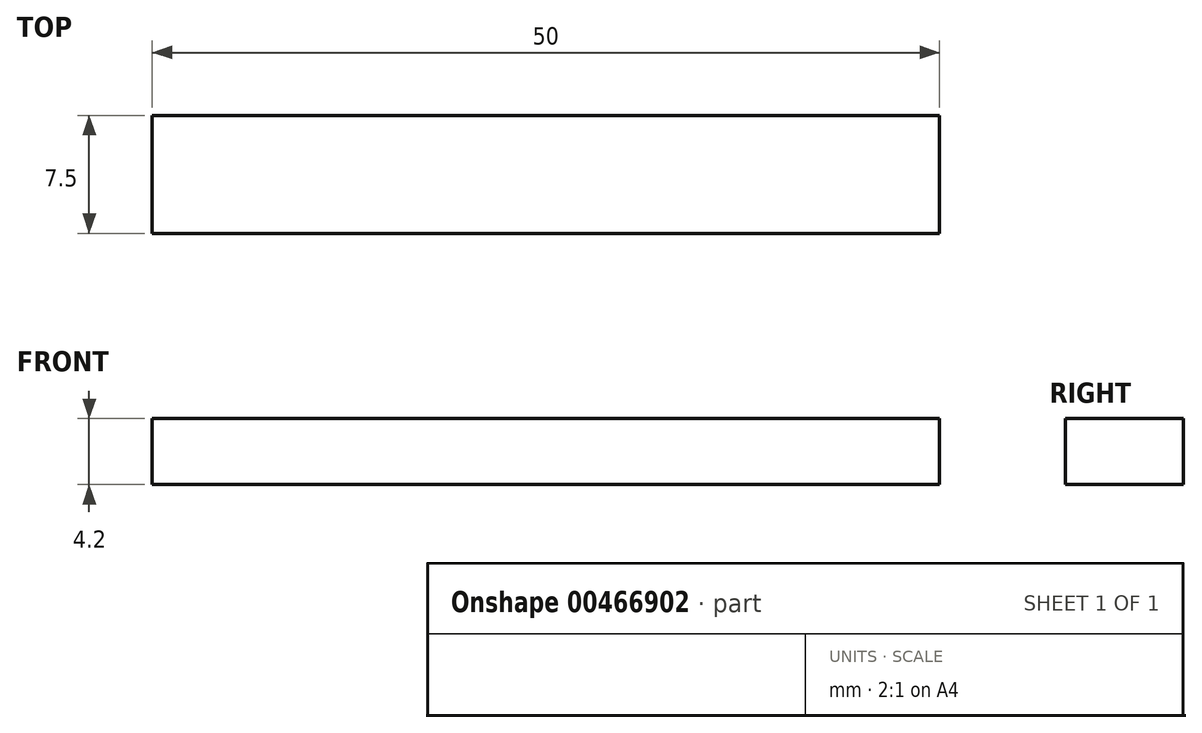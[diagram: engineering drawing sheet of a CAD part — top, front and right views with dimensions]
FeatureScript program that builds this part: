
annotation { "Feature Type Name" : "Feature", "Feature Type Description" : "" }
export const myFeature = defineFeature(function(context is Context, id is Id, definition is map)
    precondition{}
    {
        {
            var Q0;
            Q0=qCreatedBy(makeId("Top.planeOp"),FACE);
            var sketch = newSketch(context, id + "F0", { "sketchPlane" : qUnion([Q0])});
            skLineSegment(sketch, "E0.bottom", {"start": v(-25, -3.75) * mm, "end": v(25, -3.75) * mm});
            skLineSegment(sketch, "E0.top", {"start": v(-25, 3.75) * mm, "end": v(25, 3.75) * mm});
            skLineSegment(sketch, "E0.left", {"start": v(-25, -3.75) * mm, "end": v(-25, 3.75) * mm});
            skLineSegment(sketch, "E0.right", {"start": v(25, -3.75) * mm, "end": v(25, 3.75) * mm});
            skPoint(sketch, "E0.middle", {"position": v(0, 0) * mm});
            skSolve(sketch);
        }
        {
            var Q0;
            Q0=qSketchRegion(id+"F0",true);
            extrude(context, id + "F1", {"entities" : qUnion([Q0]), "depth" : 4.2 * mm});
        }
        {
            var Q0;
            Q0 = qSketchRegion(id + "F0", true);
            extrude(context, id + "F2", {"entities" : qUnion([Q0]), "operationType" : NewBodyOperationType.ADD, "depth" : 4.2 * mm});
        }
    });
